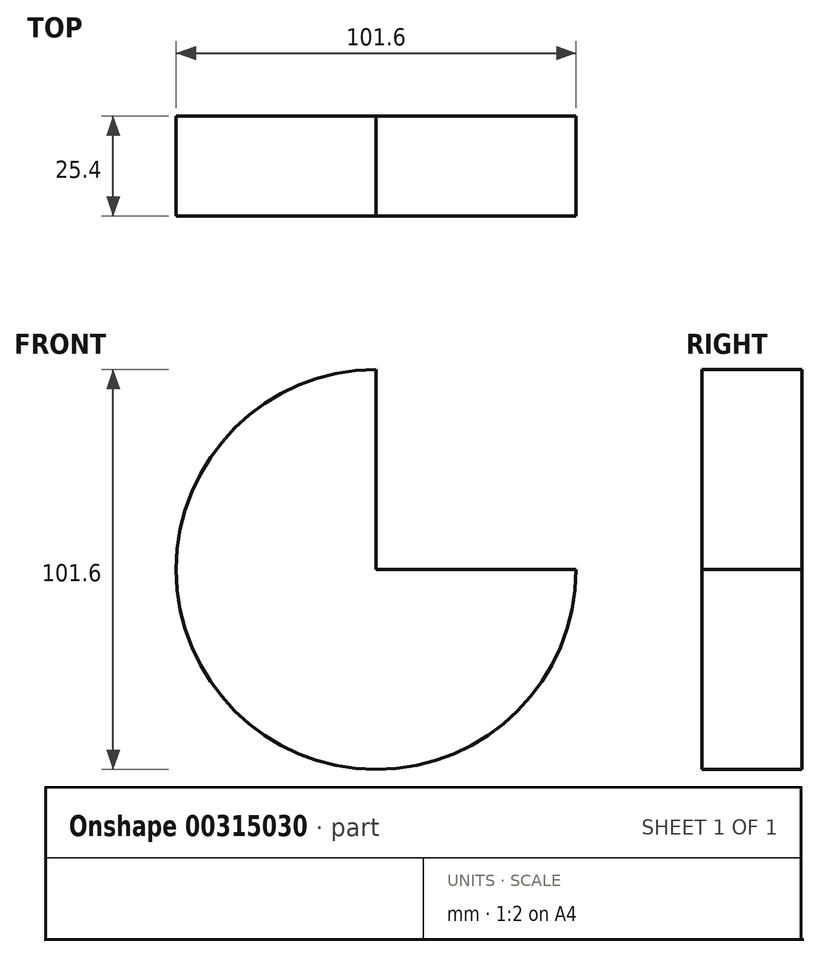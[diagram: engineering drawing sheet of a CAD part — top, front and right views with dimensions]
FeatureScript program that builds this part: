
annotation { "Feature Type Name" : "Feature", "Feature Type Description" : "" }
export const myFeature = defineFeature(function(context is Context, id is Id, definition is map)
    precondition{}
    {
        {
            var Q0;
            Q0=qCreatedBy(makeId("Front.planeOp"),FACE);
            var sketch = newSketch(context, id + "F0", { "sketchPlane" : qUnion([Q0])});
            skArc(sketch, "E0", {"start": v(0, 50.8) * mm, "mid": v(-35.92, -35.92) * mm, "end": v(50.8, 0) * mm});
            skLineSegment(sketch, "E1", {"start": v(0, 0) * mm, "end": v(0, 50.8) * mm});
            skLineSegment(sketch, "E2", {"start": v(0, 0) * mm, "end": v(50.8, 0) * mm});
            skSolve(sketch);
        }
        {
            var Q0;
            Q0=makeQuery(id+"F0.imprint","IMPRINT",FACE,{"disambiguationData":[TD([[makeQuery(id+"F0.imprint","IMPRINT",EDGE,{"derivedFrom":sQuery(id+"F0.wireOp",EDGE,"E0")}),1.0]])]});
            extrude(context, id + "F1", {"entities" : qUnion([Q0]), "depth" : 25.4 * mm});
        }
    });
